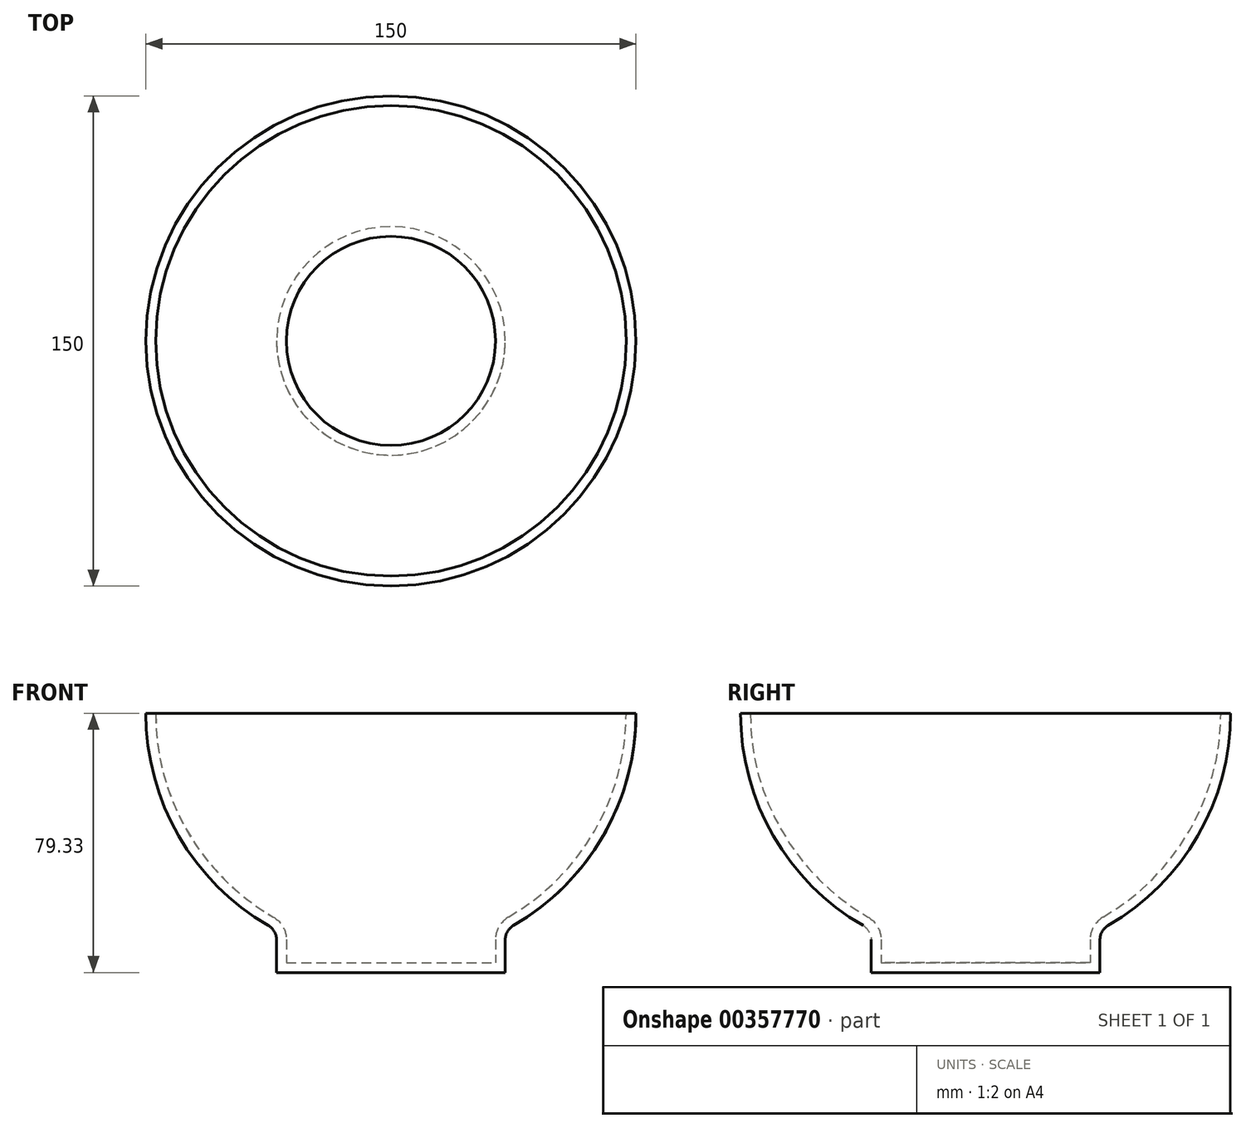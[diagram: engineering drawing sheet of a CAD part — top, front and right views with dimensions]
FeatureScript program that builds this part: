
annotation { "Feature Type Name" : "Feature", "Feature Type Description" : "" }
export const myFeature = defineFeature(function(context is Context, id is Id, definition is map)
    precondition{}
    {
        {
            var Q0;
            Q0=qCreatedBy(makeId("Front.planeOp"),FACE);
            var sketch = newSketch(context, id + "F0", { "sketchPlane" : qUnion([Q0])});
            skLineSegment(sketch, "E0", {"start": v(0, 0) * mm, "end": v(35, 0) * mm});
            skLineSegment(sketch, "E1", {"start": v(35, 0) * mm, "end": v(35, 13) * mm});
            skLineSegment(sketch, "E2", {"start": v(0, 0) * mm, "end": v(0, 79.33) * mm});
            skLineSegment(sketch, "E3", {"start": v(0, 79.33) * mm, "end": v(75, 79.33) * mm});
            skArc(sketch, "E4", {"start": v(35, 13) * mm, "mid": v(64.23, 40.6) * mm, "end": v(75, 79.33) * mm});
            skSolve(sketch);
        }
        {
            var Q0;
            Q0=makeQuery(id+"F0.imprint","IMPRINT",FACE,{"disambiguationData":[TD([[makeQuery(id+"F0.imprint","IMPRINT",EDGE,{"derivedFrom":sQuery(id+"F0.wireOp",EDGE,"E0")}),1.0]])]});
            var Q1;
            Q1=sQuery(id+"F0.wireOp",EDGE,"E2");
            revolve(context, id + "F1", {"entities" : qUnion([Q0]), "axis" : qUnion([Q1]), "revolveType" : RevolveType.FULL});
        }
        {
            var Q0;
            Q0=makeQuery(id+"F1.opRevolve","SWEPT_EDGE",EDGE,{"disambiguationData":[OSD([sQuery(id+"F0.wireOp",EDGE,"E1"),sQuery(id+"F0.wireOp",EDGE,"E4")])]});
            fillet(context, id + "F2", {"entities" : qUnion([Q0]), "radius" : 5 * mm, "tangentPropagation" : true, "allowEdgeOverflow" : false});
        }
        {
            var Q0;
            Q0=makeQuery(id+"F1.opRevolve","SWEPT_FACE",FACE,{"disambiguationData":[OSD([sQuery(id+"F0.wireOp",EDGE,"E3")])]});
            shell(context, id + "F3", {"entities" : qUnion([Q0]), "thickness" : 3 * mm});
        }
    });
